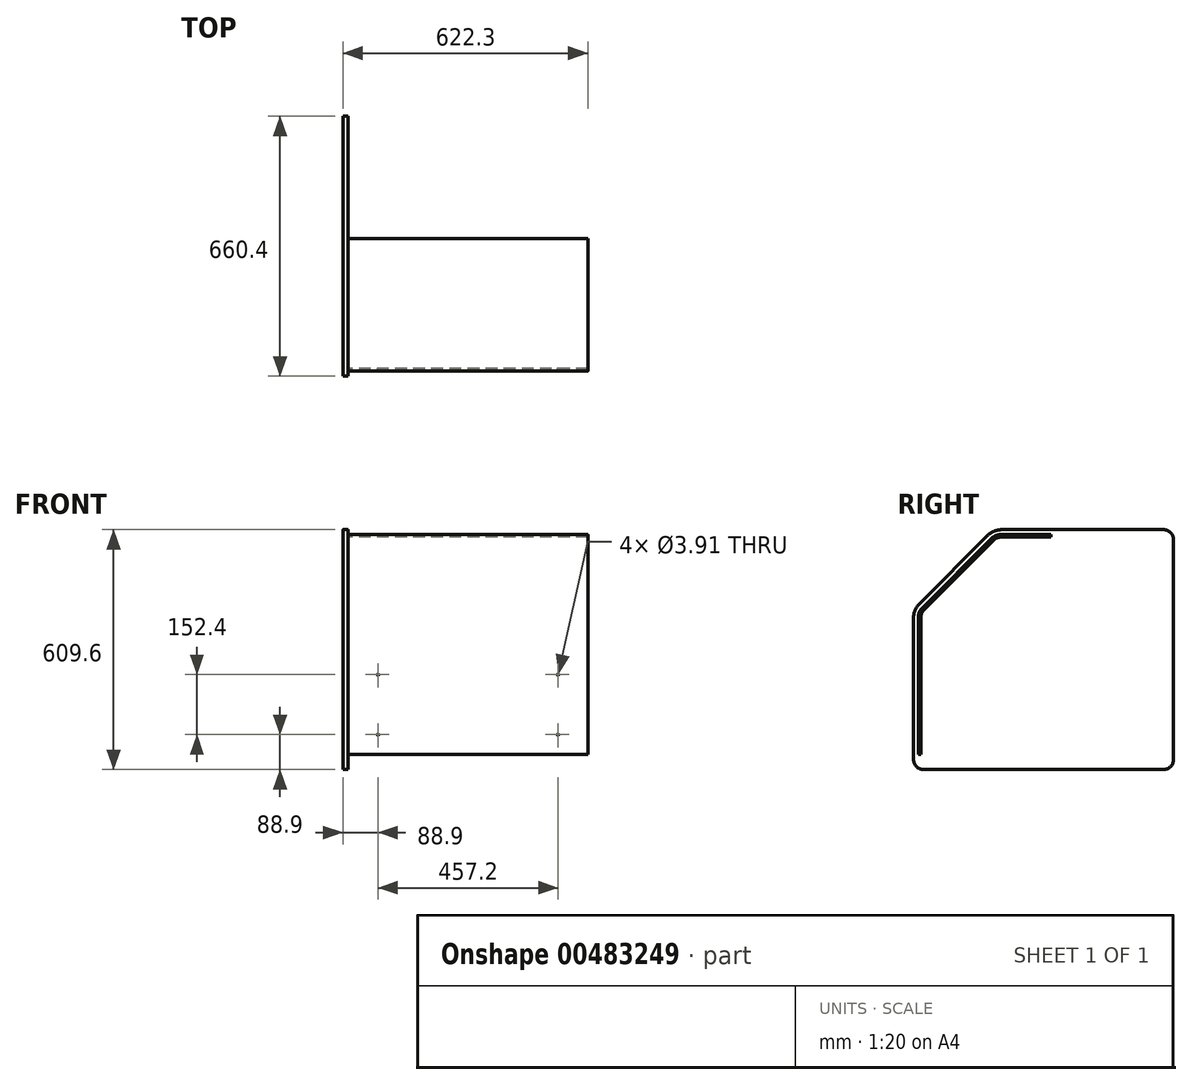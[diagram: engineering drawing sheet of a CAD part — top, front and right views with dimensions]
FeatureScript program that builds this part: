
annotation { "Feature Type Name" : "Feature", "Feature Type Description" : "" }
export const myFeature = defineFeature(function(context is Context, id is Id, definition is map)
    precondition{}
    {
        {
            var Q0;
            Q0=qCreatedBy(makeId("Right.planeOp"),FACE);
            var sketch = newSketch(context, id + "F0", { "sketchPlane" : qUnion([Q0])});
            skLineSegment(sketch, "E0.bottom", {"start": v(304.8, 304.8) * mm, "end": v(-105.96, 304.8) * mm});
            skLineSegment(sketch, "E0.top", {"start": v(304.8, -304.8) * mm, "end": v(-304.8, -304.8) * mm});
            skLineSegment(sketch, "E0.left", {"start": v(330.2, 279.4) * mm, "end": v(330.2, -279.4) * mm});
            skLineSegment(sketch, "E0.right", {"start": v(-330.2, 80.56) * mm, "end": v(-330.2, -279.4) * mm});
            skPoint(sketch, "E0.middle", {"position": v(0, 0) * mm});
            skLineSegment(sketch, "E1", {"start": v(-315.32, 116.48) * mm, "end": v(-141.88, 289.92) * mm});
            skPoint(sketch, "E2.orphan", {"position": v(-330.2, 304.8) * mm});
            skPoint(sketch, "E3.visualSharp", {"position": v(-127, 304.8) * mm});
            skArc(sketch, "E3.filletArc", {"start": v(-105.96, 304.8) * mm, "mid": v(-125.4, 300.93) * mm, "end": v(-141.88, 289.92) * mm});
            skPoint(sketch, "E4.visualSharp", {"position": v(-330.2, 101.6) * mm});
            skArc(sketch, "E4.filletArc", {"start": v(-315.32, 116.48) * mm, "mid": v(-326.33, 100) * mm, "end": v(-330.2, 80.56) * mm});
            skPoint(sketch, "E5.visualSharp", {"position": v(330.2, 304.8) * mm});
            skArc(sketch, "E5.filletArc", {"start": v(330.2, 279.4) * mm, "mid": v(322.76, 297.36) * mm, "end": v(304.8, 304.8) * mm});
            skPoint(sketch, "E6.visualSharp", {"position": v(-330.2, -304.8) * mm});
            skArc(sketch, "E6.filletArc", {"start": v(-330.2, -279.4) * mm, "mid": v(-322.76, -297.36) * mm, "end": v(-304.8, -304.8) * mm});
            skPoint(sketch, "E7.visualSharp", {"position": v(330.2, -304.8) * mm});
            skArc(sketch, "E7.filletArc", {"start": v(304.8, -304.8) * mm, "mid": v(322.76, -297.36) * mm, "end": v(330.2, -279.4) * mm});
            skSolve(sketch);
        }
        {
            var Q0;
            Q0=qSketchRegion(id+"F0",true);
            extrude(context, id + "F1", {"entities" : qUnion([Q0]), "depth" : 12.7 * mm});
        }
        {
            var Q0;
            Q0=makeQuery(id+"F1.opExtrude","CAP_FACE",FACE,{"disambiguationData":[OSD([sQuery(id+"F0.wireOp",EDGE,"E0.bottom"),sQuery(id+"F0.wireOp",EDGE,"E0.top"),sQuery(id+"F0.wireOp",EDGE,"E0.left"),sQuery(id+"F0.wireOp",EDGE,"E0.right"),sQuery(id+"F0.wireOp",EDGE,"E1"),sQuery(id+"F0.wireOp",EDGE,"E3.filletArc"),sQuery(id+"F0.wireOp",EDGE,"E4.filletArc"),sQuery(id+"F0.wireOp",EDGE,"E5.filletArc"),sQuery(id+"F0.wireOp",EDGE,"E6.filletArc"),sQuery(id+"F0.wireOp",EDGE,"E7.filletArc")])],"isStart":false});
            var sketch = newSketch(context, id + "F2", { "sketchPlane" : qUnion([Q0])});
            skLineSegment(sketch, "E8.1", {"start": v(-317.5, 85.82) * mm, "end": v(-317.5, -266.7) * mm});
            skLineSegment(sketch, "E8.3", {"start": v(19.05, 292.1) * mm, "end": v(-111.22, 292.1) * mm});
            skLineSegment(sketch, "E8.4", {"start": v(-129.18, 284.66) * mm, "end": v(-310.06, 103.78) * mm});
            skLineSegment(sketch, "E9.0", {"start": v(-311.15, 83.19) * mm, "end": v(-311.15, -266.7) * mm});
            skLineSegment(sketch, "E9.1", {"start": v(-126.55, 278.31) * mm, "end": v(-303.71, 101.15) * mm});
            skLineSegment(sketch, "E9.4", {"start": v(19.05, 285.75) * mm, "end": v(-108.59, 285.75) * mm});
            skLineSegment(sketch, "E10", {"start": v(19.05, 292.1) * mm, "end": v(19.05, 285.75) * mm});
            skLineSegment(sketch, "E11", {"start": v(-317.5, -266.7) * mm, "end": v(-311.15, -266.7) * mm});
            skPoint(sketch, "E12.visualSharp", {"position": v(-317.5, 96.34) * mm});
            skArc(sketch, "E12.filletArc", {"start": v(-310.06, 103.78) * mm, "mid": v(-315.57, 95.54) * mm, "end": v(-317.5, 85.82) * mm});
            skPoint(sketch, "E13.visualSharp", {"position": v(-311.15, 93.7) * mm});
            skArc(sketch, "E13.filletArc", {"start": v(-303.71, 101.15) * mm, "mid": v(-309.22, 92.9) * mm, "end": v(-311.15, 83.19) * mm});
            skPoint(sketch, "E14.visualSharp", {"position": v(-121.74, 292.1) * mm});
            skArc(sketch, "E14.filletArc", {"start": v(-111.22, 292.1) * mm, "mid": v(-120.94, 290.17) * mm, "end": v(-129.18, 284.66) * mm});
            skPoint(sketch, "E15.visualSharp", {"position": v(-119.1, 285.75) * mm});
            skArc(sketch, "E15.filletArc", {"start": v(-108.59, 285.75) * mm, "mid": v(-118.3, 283.82) * mm, "end": v(-126.55, 278.31) * mm});
            skSolve(sketch);
        }
        {
            var Q0;
            Q0 = qSketchRegion(id + "F2", true);
            extrude(context, id + "F3", {"entities" : qUnion([Q0]), "depth" : 609.6 * mm});
        }
        {
            var Q0;
            Q0=makeQuery(id+"F3.opExtrude","SWEPT_FACE",FACE,{"disambiguationData":[OSD([sQuery(id+"F2.wireOp",EDGE,"E8.1")])]});
            var sketch = newSketch(context, id + "F4", { "sketchPlane" : qUnion([Q0])});
            skCircle(sketch, "E16", {"center": v(546.1, -215.9) * mm, "radius": 1.96 * mm});
            skCircle(sketch, "E17", {"center": v(546.1, -63.5) * mm, "radius": 1.96 * mm});
            skCircle(sketch, "E18", {"center": v(88.9, -63.5) * mm, "radius": 1.96 * mm});
            skCircle(sketch, "E19", {"center": v(88.9, -215.9) * mm, "radius": 1.96 * mm});
            skSolve(sketch);
        }
        {
            var Q0;
            Q0 = qSketchRegion(id + "F4", true);
            extrude(context, id + "F5", {"entities" : qUnion([Q0]), "operationType" : NewBodyOperationType.REMOVE, "endBound" : BoundingType.THROUGH_ALL, "oppositeDirection" : true, "depth" : 25.4 * mm});
        }
    });
